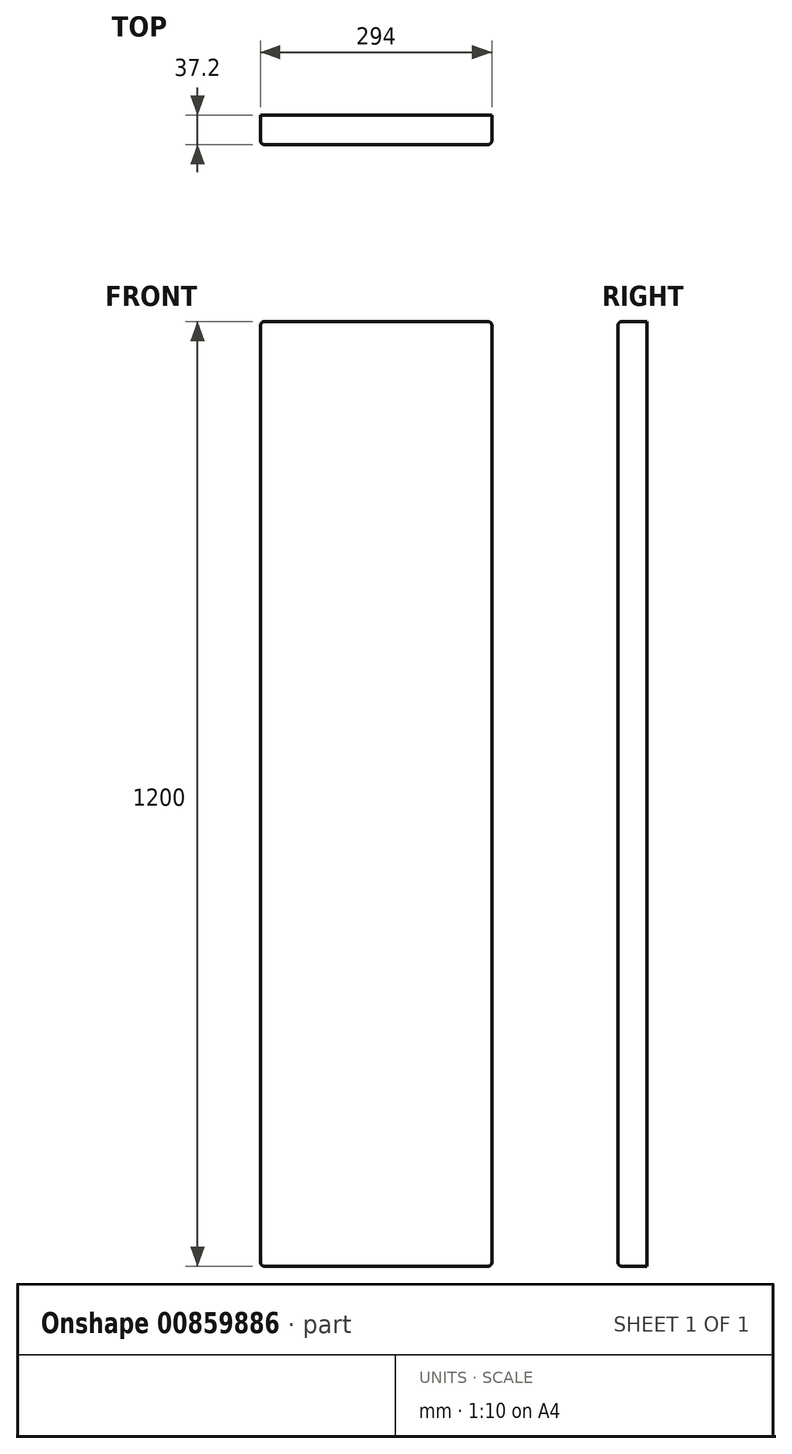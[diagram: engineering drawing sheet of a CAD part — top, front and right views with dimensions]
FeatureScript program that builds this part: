
annotation { "Feature Type Name" : "Feature", "Feature Type Description" : "" }
export const myFeature = defineFeature(function(context is Context, id is Id, definition is map)
    precondition{}
    {
        {
            var Q0;
            Q0=qCreatedBy(makeId("Front.planeOp"),FACE);
            var sketch = newSketch(context, id + "F0", { "sketchPlane" : qUnion([Q0])});
            skLineSegment(sketch, "E0.bottom", {"start": v(147, 600) * mm, "end": v(-147, 600) * mm});
            skLineSegment(sketch, "E0.top", {"start": v(147, -600) * mm, "end": v(-147, -600) * mm});
            skLineSegment(sketch, "E0.left", {"start": v(147, 600) * mm, "end": v(147, -600) * mm});
            skLineSegment(sketch, "E0.right", {"start": v(-147, 600) * mm, "end": v(-147, -600) * mm});
            skPoint(sketch, "E0.middle", {"position": v(0, 0) * mm});
            skSolve(sketch);
        }
        {
            var Q0;
            Q0=makeQuery(id+"F0.imprint","IMPRINT",FACE,{"disambiguationData":[TD([[makeQuery(id+"F0.imprint","IMPRINT",EDGE,{"derivedFrom":sQuery(id+"F0.wireOp",EDGE,"E0.bottom")}),1.0]])]});
            extrude(context, id + "F1", {"entities" : qUnion([Q0]), "depth" : 37.2 * mm, "offsetDistance" : 25 * mm});
        }
        {
            var Q0;
            Q0=makeQuery(id+"F1.opExtrude","CAP_FACE",FACE,{"disambiguationData":[OSD([sQuery(id+"F0.wireOp",EDGE,"E0.bottom"),sQuery(id+"F0.wireOp",EDGE,"E0.top"),sQuery(id+"F0.wireOp",EDGE,"E0.left"),sQuery(id+"F0.wireOp",EDGE,"E0.right")])],"isStart":false});
            var Q1;
            Q1=makeQuery(id+"F1.opExtrude","SWEPT_EDGE",EDGE,{"disambiguationData":[OSD([sQuery(id+"F0.wireOp",EDGE,"E0.bottom"),sQuery(id+"F0.wireOp",EDGE,"E0.right")])]});
            var Q2;
            Q2=makeQuery(id+"F1.opExtrude","SWEPT_EDGE",EDGE,{"disambiguationData":[OSD([sQuery(id+"F0.wireOp",EDGE,"E0.bottom"),sQuery(id+"F0.wireOp",EDGE,"E0.left")])]});
            var Q3;
            Q3=makeQuery(id+"F1.opExtrude","SWEPT_EDGE",EDGE,{"disambiguationData":[OSD([sQuery(id+"F0.wireOp",EDGE,"E0.top"),sQuery(id+"F0.wireOp",EDGE,"E0.left")])]});
            var Q4;
            Q4=makeQuery(id+"F1.opExtrude","SWEPT_EDGE",EDGE,{"disambiguationData":[OSD([sQuery(id+"F0.wireOp",EDGE,"E0.top"),sQuery(id+"F0.wireOp",EDGE,"E0.right")])]});
            fillet(context, id + "F2", {"entities" : qUnion([Q0, Q1, Q2, Q3, Q4]), "radius" : 5 * mm, "tangentPropagation" : true, "allowEdgeOverflow" : false});
        }
    });
